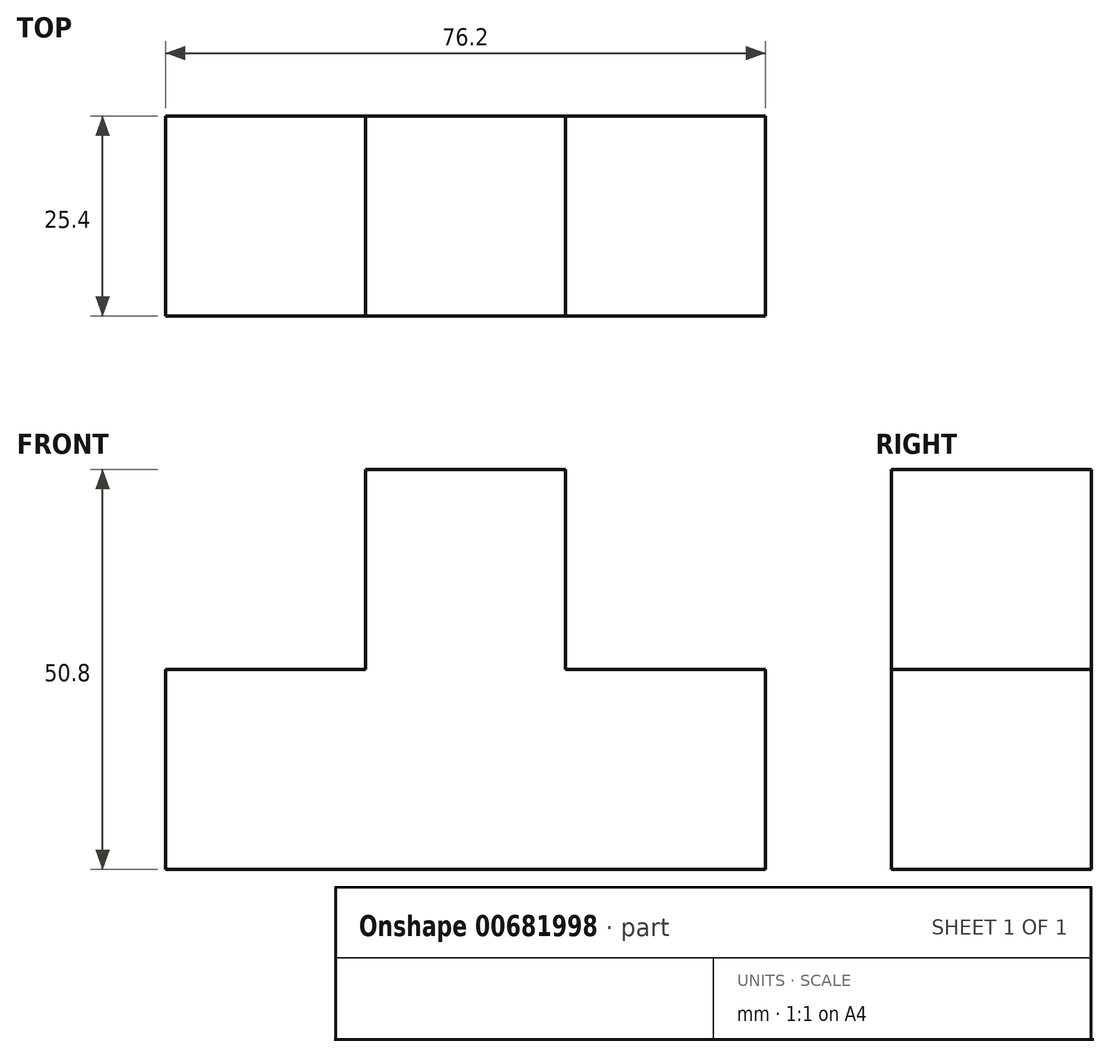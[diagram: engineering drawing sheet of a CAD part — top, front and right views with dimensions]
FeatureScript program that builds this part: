
annotation { "Feature Type Name" : "Feature", "Feature Type Description" : "" }
export const myFeature = defineFeature(function(context is Context, id is Id, definition is map)
    precondition{}
    {
        {
            var Q0;
            Q0=qCreatedBy(makeId("Front.planeOp"),FACE);
            var sketch = newSketch(context, id + "F0", { "sketchPlane" : qUnion([Q0])});
            skLineSegment(sketch, "E0", {"start": v(34.29, 0) * mm, "end": v(-41.91, 0) * mm});
            skLineSegment(sketch, "E1", {"start": v(-41.91, 0) * mm, "end": v(-41.91, 25.4) * mm});
            skLineSegment(sketch, "E2", {"start": v(-41.91, 25.4) * mm, "end": v(-16.51, 25.4) * mm});
            skLineSegment(sketch, "E3", {"start": v(-16.51, 25.4) * mm, "end": v(-16.51, 50.8) * mm});
            skLineSegment(sketch, "E4", {"start": v(-16.51, 50.8) * mm, "end": v(8.89, 50.8) * mm});
            skLineSegment(sketch, "E5", {"start": v(8.89, 50.8) * mm, "end": v(8.89, 25.4) * mm});
            skLineSegment(sketch, "E6", {"start": v(8.89, 25.4) * mm, "end": v(34.29, 25.4) * mm});
            skLineSegment(sketch, "E7", {"start": v(34.29, 25.4) * mm, "end": v(34.29, 0) * mm});
            skSolve(sketch);
        }
        {
            var Q0;
            Q0=makeQuery(id+"F0.imprint","IMPRINT",FACE,{"disambiguationData":[TD([[makeQuery(id+"F0.imprint","IMPRINT",EDGE,{"derivedFrom":sQuery(id+"F0.wireOp",EDGE,"E0")}),-1.0]])]});
            extrude(context, id + "F1", {"entities" : qUnion([Q0]), "depth" : 25.4 * mm, "offsetDistance" : 25.4 * mm});
        }
    });
